# Revit family: 3-504-14 Reflex
name_source: partatom
category: Lighting Fixtures
revit_build: Autodesk Revit LT 2015 (Build: 20140606_1530(x64)
units: mm (PartAtom-declared; Revit-internal decimal feet)

## types (1)
- 3-504-14 Reflex
    ADA Compliant = Yes
    Apparent Load = 14 VA
    Color Filter = 16777215
    Default Elevation = 4' - 0"
    Description = 20" wall sconce
    Diffuser = Glass
    Dimming Lamp Color Temperature Shift = <None>
    Emit Shape Visible in Rendering = No
    Emit from Rectangle Length = 0' - 3"
    Emit from Rectangle Width = 0' - 3"
    Fixture Depth = 0' - 3 9/16"
    Fixture Height = 1' - 8"
    Fixture Width = 0' - 4"
    Input Current (A) = 0.165
    Input Power (W) = 14.3
    Input Voltage (V) = 120
    Junction Box = 2"x3" J-Box, 4" octagonal w.optional backplate
    Lamp = 2x7W GU10 LED
    Lamp Manufacturer = Lamp not supplied by manufacturer
    Manufacturer = Oxygen Lighting.com
    Metal Finish = 14-Polished Chrome
    Model = 3-204-14
    Photometric Web File = Reflex 3-504-xx ITL82260.IES
    Power Factor = 0.722
    Tilt Angle = 90.00°
    Type Comments = Lighting - LED
    URL = http://www.oxygenlighting.com

## geometry (parser evidence)
native form markers: Sweep x3
no freeform markers — native parametric forms only
